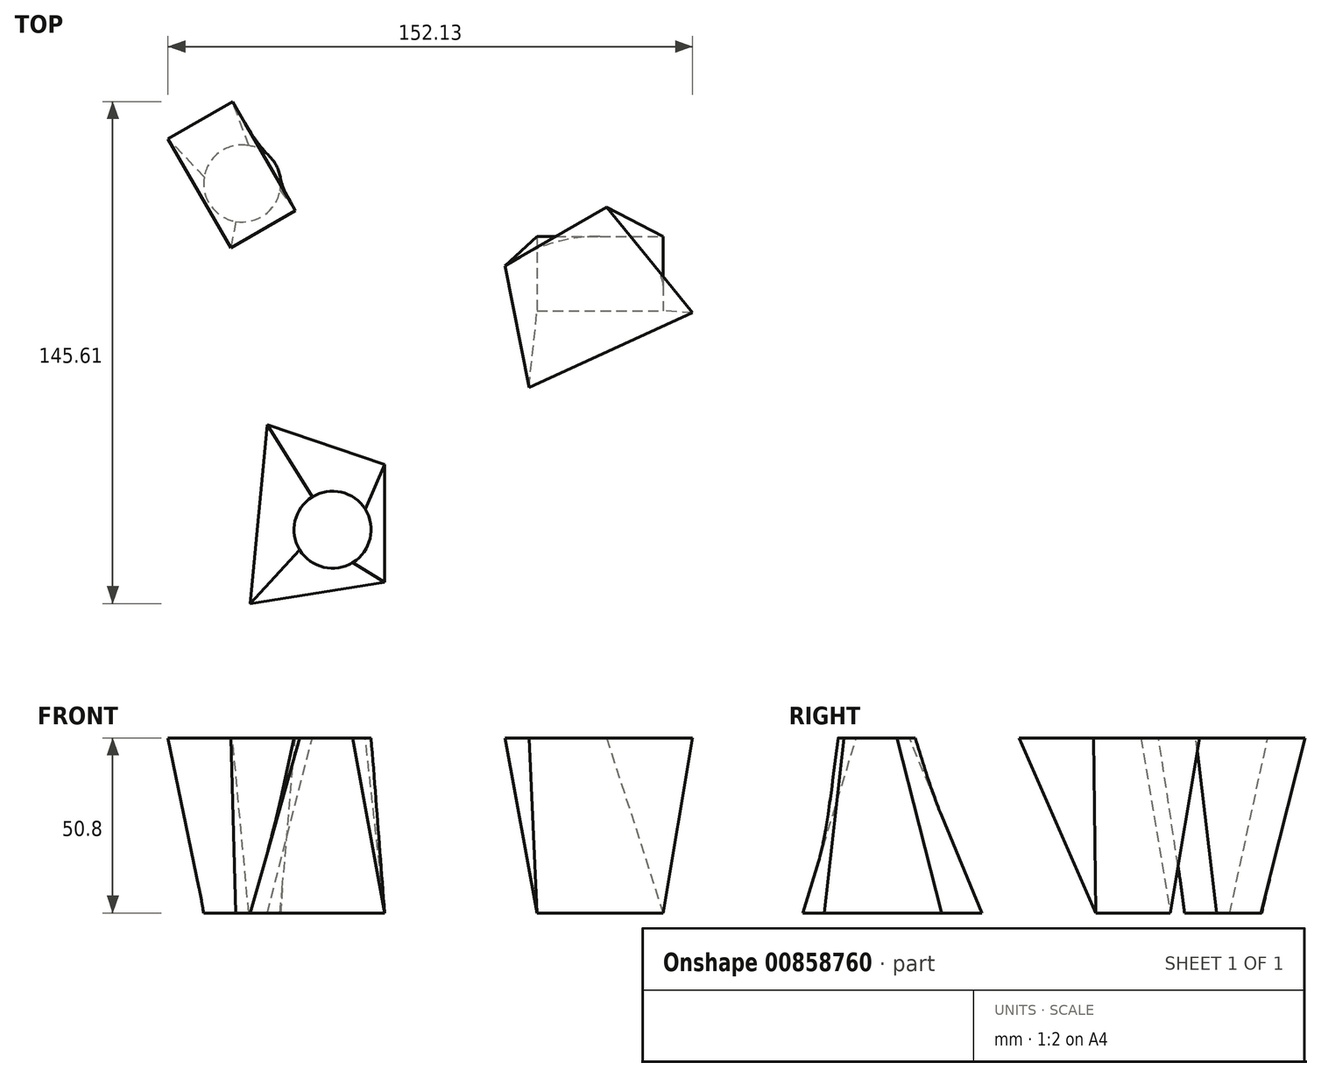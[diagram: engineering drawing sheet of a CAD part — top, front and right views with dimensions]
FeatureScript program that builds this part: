
annotation { "Feature Type Name" : "Feature", "Feature Type Description" : "" }
export const myFeature = defineFeature(function(context is Context, id is Id, definition is map)
    precondition{}
    {
        {
            var Q0;
            Q0=qCreatedBy(makeId("Top.planeOp"),FACE);
            var sketch = newSketch(context, id + "F0", { "sketchPlane" : qUnion([Q0])});
            skCircle(sketch, "E0", {"center": v(-62.28, 52.52) * mm, "radius": 11.18 * mm});
            skLineSegment(sketch, "E1.bottom", {"start": v(23.25, 37.16) * mm, "end": v(59.79, 37.16) * mm});
            skLineSegment(sketch, "E1.top", {"start": v(23.25, 15.57) * mm, "end": v(59.79, 15.57) * mm});
            skLineSegment(sketch, "E1.left", {"start": v(23.25, 37.16) * mm, "end": v(23.25, 15.57) * mm});
            skLineSegment(sketch, "E1.right", {"start": v(59.79, 37.16) * mm, "end": v(59.79, 15.57) * mm});
            skLineSegment(sketch, "E2", {"start": v(-55, -17.45) * mm, "end": v(-20.95, -29.08) * mm});
            skLineSegment(sketch, "E3", {"start": v(-20.95, -29.08) * mm, "end": v(-20.95, -63.13) * mm});
            skLineSegment(sketch, "E4", {"start": v(-20.95, -63.13) * mm, "end": v(-59.98, -69.35) * mm});
            skLineSegment(sketch, "E5", {"start": v(-59.98, -69.35) * mm, "end": v(-55, -17.45) * mm});
            skLineSegment(sketch, "E6", {"start": v(-82.91, 71.7) * mm, "end": v(-82.91, 30.26) * mm, "construction": true});
            skSolve(sketch);
        }
        {
            var Q0;
            Q0=qCreatedBy(makeId("Top.planeOp"),FACE);
            cPlane(context, id + "F1", {"entities" : qUnion([Q0]), "cplaneType" : CPlaneType.OFFSET, "offset" : 50.8 * mm, "width" : 152.4 * mm, "height" : 152.4 * mm});
        }
        {
            var Q0;
            Q0=qCreatedBy(id+"F1.planeOp",FACE);
            var sketch = newSketch(context, id + "F2", { "sketchPlane" : qUnion([Q0])});
            skCircle(sketch, "E7.0", {"center": v(-36.07, -47.94) * mm, "radius": 11.18 * mm});
            skLineSegment(sketch, "E7.1.0", {"start": v(-65.53, 33.82) * mm, "end": v(-46.83, 44.61) * mm});
            skLineSegment(sketch, "E7.1.1", {"start": v(-46.83, 44.61) * mm, "end": v(-65.1, 76.26) * mm});
            skLineSegment(sketch, "E7.1.2", {"start": v(-65.1, 76.26) * mm, "end": v(-83.8, 65.46) * mm});
            skLineSegment(sketch, "E7.1.3", {"start": v(-83.8, 65.46) * mm, "end": v(-65.53, 33.82) * mm});
            skLineSegment(sketch, "E7.2.0", {"start": v(20.9, -6.64) * mm, "end": v(68.33, 15) * mm});
            skLineSegment(sketch, "E7.2.1", {"start": v(68.33, 15) * mm, "end": v(43.42, 45.68) * mm});
            skLineSegment(sketch, "E7.2.2", {"start": v(43.42, 45.68) * mm, "end": v(13.94, 28.66) * mm});
            skLineSegment(sketch, "E7.2.3", {"start": v(13.94, 28.66) * mm, "end": v(20.9, -6.64) * mm});
            skSolve(sketch);
        }
        {
            var Q0;
            Q0=makeQuery(id+"F2.imprint","IMPRINT",FACE,{"disambiguationData":[TD([[makeQuery(id+"F2.imprint","IMPRINT",EDGE,{"derivedFrom":sQuery(id+"F2.wireOp",EDGE,"E7.2.0")}),1.0]])]});
            var Q1;
            Q1=makeQuery(id+"F0.imprint","IMPRINT",FACE,{"disambiguationData":[TD([[makeQuery(id+"F0.imprint","IMPRINT",EDGE,{"derivedFrom":sQuery(id+"F0.wireOp",EDGE,"E1.bottom")}),-1.0]])]});
            loft(context, id + "F3", {"sheetProfilesArray" : [{ "sheetProfileEntities" : qUnion([Q0]) }, { "sheetProfileEntities" : qUnion([Q1]) }]});
        }
        {
            var Q0;
            Q0=makeQuery(id+"F0.imprint","IMPRINT",FACE,{"disambiguationData":[TD([[makeQuery(id+"F0.imprint","IMPRINT",EDGE,{"derivedFrom":sQuery(id+"F0.wireOp",EDGE,"E2")}),-1.0]])]});
            var Q1;
            Q1=makeQuery(id+"F2.imprint","IMPRINT",FACE,{"disambiguationData":[TD([[makeQuery(id+"F2.imprint","IMPRINT",EDGE,{"derivedFrom":sQuery(id+"F2.wireOp",EDGE,"E7.0")}),1.0]])]});
            loft(context, id + "F4", {"sheetProfilesArray" : [{ "sheetProfileEntities" : qUnion([Q0]) }, { "sheetProfileEntities" : qUnion([Q1]) }]});
        }
        {
            var Q0;
            Q0=makeQuery(id+"F0.imprint","IMPRINT",FACE,{"disambiguationData":[TD([[makeQuery(id+"F0.imprint","IMPRINT",EDGE,{"derivedFrom":sQuery(id+"F0.wireOp",EDGE,"E0")}),1.0]])]});
            var Q1;
            Q1=makeQuery(id+"F2.imprint","IMPRINT",FACE,{"disambiguationData":[TD([[makeQuery(id+"F2.imprint","IMPRINT",EDGE,{"derivedFrom":sQuery(id+"F2.wireOp",EDGE,"E7.1.0")}),1.0]])]});
            loft(context, id + "F5", {"sheetProfilesArray" : [{ "sheetProfileEntities" : qUnion([Q0]) }, { "sheetProfileEntities" : qUnion([Q1]) }]});
        }
    });
